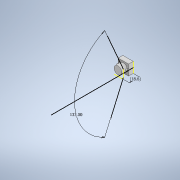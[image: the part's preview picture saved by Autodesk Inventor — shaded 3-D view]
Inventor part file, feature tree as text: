
AUTODESK INVENTOR PART (.ipt)
format: ipt  version: 2020 (Build 240168000, 168)  size: 155,136 bytes
history: native  units: in
note: dims shown in document units (in); Inventor stores cm internally (conversion verified against a paired STEP export)
features: sketch x5, extrude x3, projected_geometry x3
ambient origin geometry x8: Origin, YZ Plane, XZ Plane, XY Plane, X Axis, Y Axis, Z Axis, Center Point
bodies: Solid1 (feature_tree)
feature tree (11):
  extrude  "Extrusion1"  Depth=0.752in
  extrude  "Extrusion2"  Depth=0.4331in
  extrude  "Extrusion3"  Depth=0.1575in
  sketch  "Sketch4"  dims[d7=0.3413in d8=0.0in]
  sketch  "Sketch5"  dims[d9=0.5512in d10=0.3909in d11=0.0in d12=0.7323in d13=0.9139in]
  sketch  "Sketch1"  dims[d0=0.752in d1=0.752in]
  sketch  "Sketch2"  dims[d2=0.3413in d3=0.0in d4=0.4331in]
  projected_geometry  "Projected Loop1"
  sketch  "Sketch3"  dims[d5=0.0787in d6=0.1575in]
  projected_geometry  "Projected Loop2"
  projected_geometry  "Projected Loop3"
